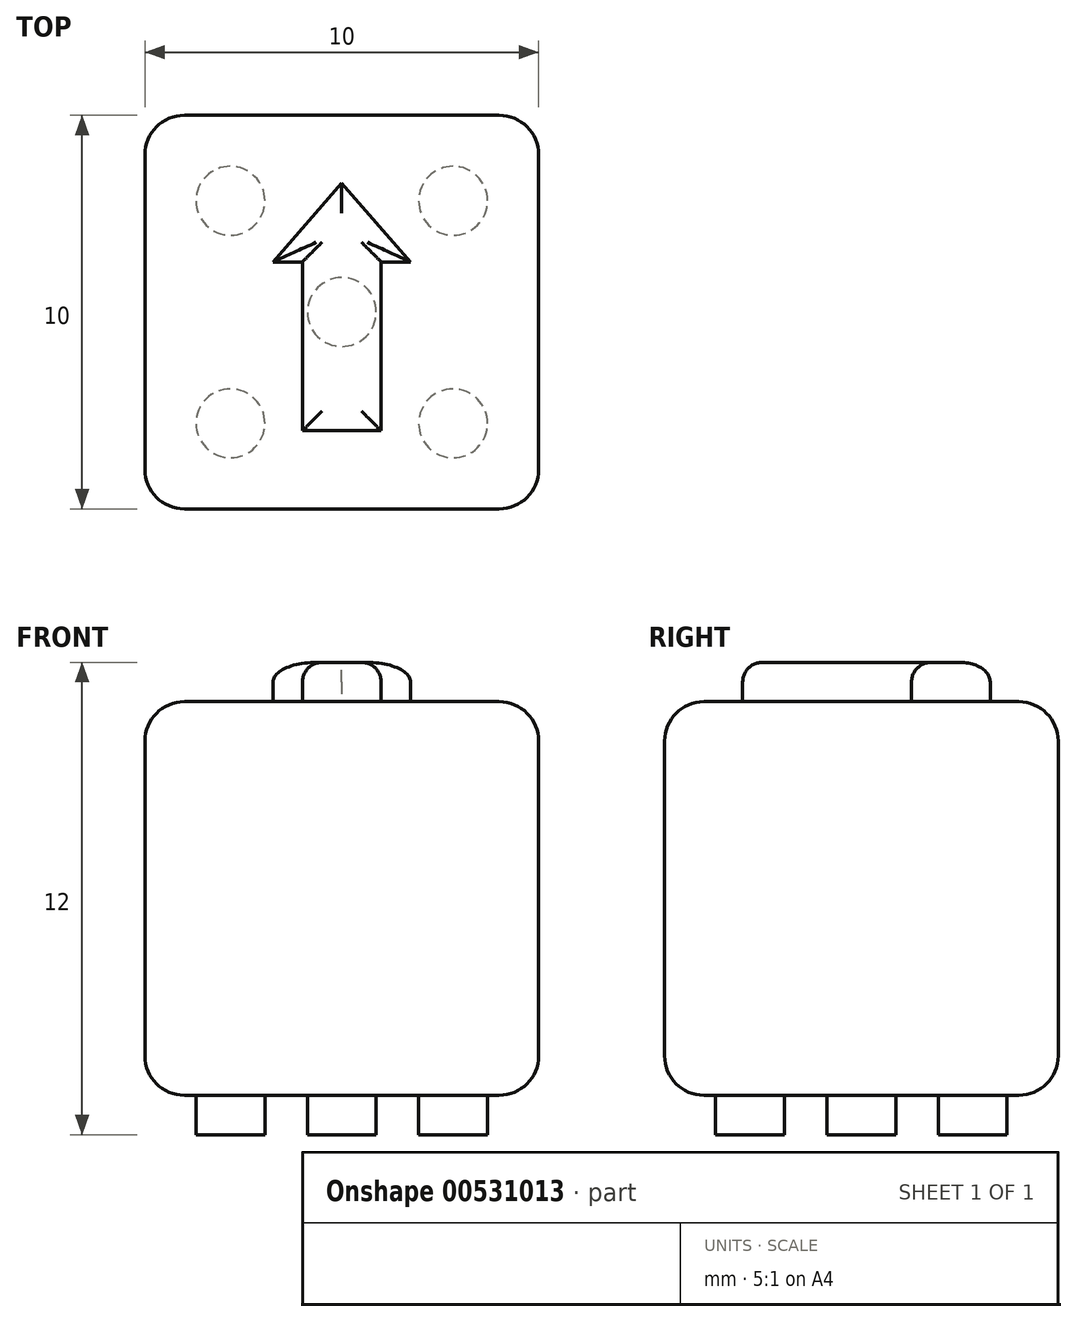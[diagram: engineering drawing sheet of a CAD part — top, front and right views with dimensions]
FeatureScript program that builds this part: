
annotation { "Feature Type Name" : "Feature", "Feature Type Description" : "" }
export const myFeature = defineFeature(function(context is Context, id is Id, definition is map)
    precondition{}
    {
        {
            var Q0;
            Q0=qCreatedBy(makeId("Top.planeOp"),FACE);
            var sketch = newSketch(context, id + "F0", { "sketchPlane" : qUnion([Q0])});
            skLineSegment(sketch, "E0.bottom", {"start": v(5, -5) * mm, "end": v(-5, -5) * mm});
            skLineSegment(sketch, "E0.top", {"start": v(5, 5) * mm, "end": v(-5, 5) * mm});
            skLineSegment(sketch, "E0.left", {"start": v(5, -5) * mm, "end": v(5, 5) * mm});
            skLineSegment(sketch, "E0.right", {"start": v(-5, -5) * mm, "end": v(-5, 5) * mm});
            skPoint(sketch, "E0.middle", {"position": v(0, 0) * mm});
            skLineSegment(sketch, "E1", {"start": v(-5, 5) * mm, "end": v(5, -5) * mm, "construction": true});
            skLineSegment(sketch, "E2", {"start": v(5, 5) * mm, "end": v(-5, -5) * mm, "construction": true});
            skCircle(sketch, "E3", {"center": v(-2.83, 2.83) * mm, "radius": 0.88 * mm});
            skCircle(sketch, "E4", {"center": v(2.83, 2.83) * mm, "radius": 0.88 * mm});
            skCircle(sketch, "E5", {"center": v(2.83, -2.83) * mm, "radius": 0.88 * mm});
            skCircle(sketch, "E6", {"center": v(-2.83, -2.83) * mm, "radius": 0.88 * mm});
            skCircle(sketch, "E7", {"center": v(0, 0) * mm, "radius": 0.88 * mm});
            skSolve(sketch);
        }
        {
            var Q0;
            Q0 = qSketchRegion(id + "F0", true);
            var Q1;
            Q1=makeQuery(id+"F0.imprint","IMPRINT",FACE,{"disambiguationData":[TD([[makeQuery(id+"F0.imprint","IMPRINT",EDGE,{"derivedFrom":sQuery(id+"F0.wireOp",EDGE,"E6")}),1.0]])]});
            var Q2;
            Q2=makeQuery(id+"F0.imprint","IMPRINT",FACE,{"disambiguationData":[TD([[makeQuery(id+"F0.imprint","IMPRINT",EDGE,{"derivedFrom":sQuery(id+"F0.wireOp",EDGE,"E3")}),1.0]])]});
            var Q3;
            Q3=makeQuery(id+"F0.imprint","IMPRINT",FACE,{"disambiguationData":[TD([[makeQuery(id+"F0.imprint","IMPRINT",EDGE,{"derivedFrom":sQuery(id+"F0.wireOp",EDGE,"E4")}),1.0]])]});
            var Q4;
            Q4=makeQuery(id+"F0.imprint","IMPRINT",FACE,{"disambiguationData":[TD([[makeQuery(id+"F0.imprint","IMPRINT",EDGE,{"derivedFrom":sQuery(id+"F0.wireOp",EDGE,"E5")}),1.0]])]});
            var Q5;
            Q5=makeQuery(id+"F0.imprint","IMPRINT",FACE,{"disambiguationData":[TD([[makeQuery(id+"F0.imprint","IMPRINT",EDGE,{"derivedFrom":sQuery(id+"F0.wireOp",EDGE,"E7")}),1.0]])]});
            extrude(context, id + "F1", {"entities" : qUnion([Q0, Q1, Q2, Q3, Q4, Q5]), "depth" : 10 * mm, "offsetDistance" : 25 * mm});
        }
        {
            var Q0;
            Q0=makeQuery(id+"F0.imprint","IMPRINT",FACE,{"disambiguationData":[TD([[makeQuery(id+"F0.imprint","IMPRINT",EDGE,{"derivedFrom":sQuery(id+"F0.wireOp",EDGE,"E4")}),1.0]])]});
            var Q1;
            Q1=makeQuery(id+"F0.imprint","IMPRINT",FACE,{"disambiguationData":[TD([[makeQuery(id+"F0.imprint","IMPRINT",EDGE,{"derivedFrom":sQuery(id+"F0.wireOp",EDGE,"E3")}),1.0]])]});
            var Q2;
            Q2=makeQuery(id+"F0.imprint","IMPRINT",FACE,{"disambiguationData":[TD([[makeQuery(id+"F0.imprint","IMPRINT",EDGE,{"derivedFrom":sQuery(id+"F0.wireOp",EDGE,"E6")}),1.0]])]});
            var Q3;
            Q3=makeQuery(id+"F0.imprint","IMPRINT",FACE,{"disambiguationData":[TD([[makeQuery(id+"F0.imprint","IMPRINT",EDGE,{"derivedFrom":sQuery(id+"F0.wireOp",EDGE,"E5")}),1.0]])]});
            var Q4;
            Q4=makeQuery(id+"F0.imprint","IMPRINT",FACE,{"disambiguationData":[TD([[makeQuery(id+"F0.imprint","IMPRINT",EDGE,{"derivedFrom":sQuery(id+"F0.wireOp",EDGE,"E7")}),1.0]])]});
            extrude(context, id + "F2", {"entities" : qUnion([Q0, Q1, Q2, Q3, Q4]), "operationType" : NewBodyOperationType.ADD, "oppositeDirection" : true, "depth" : 1 * mm, "offsetDistance" : 25 * mm});
        }
        {
            var Q0;
            Q0=makeQuery(id+"F1.opExtrude","SWEPT_EDGE",EDGE,{"disambiguationData":[OSD([sQuery(id+"F0.wireOp",EDGE,"E0.top"),sQuery(id+"F0.wireOp",EDGE,"E0.left")])]});
            var Q1;
            Q1=makeQuery(id+"F1.opExtrude","CAP_EDGE",EDGE,{"disambiguationData":[OSD([sQuery(id+"F0.wireOp",EDGE,"E0.top")])],"isStart":true});
            var Q2;
            Q2=makeQuery(id+"F1.opExtrude","CAP_EDGE",EDGE,{"disambiguationData":[OSD([sQuery(id+"F0.wireOp",EDGE,"E0.left")])],"isStart":true});
            var Q3;
            Q3=makeQuery(id+"F1.opExtrude","CAP_EDGE",EDGE,{"disambiguationData":[OSD([sQuery(id+"F0.wireOp",EDGE,"E0.right")])],"isStart":true});
            var Q4;
            Q4=makeQuery(id+"F1.opExtrude","SWEPT_FACE",FACE,{"disambiguationData":[OSD([sQuery(id+"F0.wireOp",EDGE,"E0.right")])]});
            var Q5;
            Q5=makeQuery(id+"F1.opExtrude","SWEPT_EDGE",EDGE,{"disambiguationData":[OSD([sQuery(id+"F0.wireOp",EDGE,"E0.top"),sQuery(id+"F0.wireOp",EDGE,"E0.right")])]});
            var Q6;
            Q6=makeQuery(id+"F1.opExtrude","CAP_FACE",FACE,{"disambiguationData":[OSD([sQuery(id+"F0.wireOp",EDGE,"E0.bottom"),sQuery(id+"F0.wireOp",EDGE,"E0.top"),sQuery(id+"F0.wireOp",EDGE,"E0.left"),sQuery(id+"F0.wireOp",EDGE,"E0.right")])],"isStart":false});
            var Q7;
            Q7=makeQuery(id+"F1.opExtrude","SWEPT_EDGE",EDGE,{"disambiguationData":[OSD([sQuery(id+"F0.wireOp",EDGE,"E0.bottom"),sQuery(id+"F0.wireOp",EDGE,"E0.left")])]});
            var Q8;
            Q8=makeQuery(id+"F1.opExtrude","CAP_EDGE",EDGE,{"disambiguationData":[OSD([sQuery(id+"F0.wireOp",EDGE,"E0.bottom")])],"isStart":true});
            fillet(context, id + "F3", {"entities" : qUnion([Q0, Q1, Q2, Q3, Q4, Q5, Q6, Q7, Q8]), "radius" : 1 * mm, "tangentPropagation" : true, "allowEdgeOverflow" : false});
        }
        {
            var Q0;
            Q0=makeQuery(id+"F1.opExtrude","CAP_FACE",FACE,{"disambiguationData":[OSD([sQuery(id+"F0.wireOp",EDGE,"E0.bottom"),sQuery(id+"F0.wireOp",EDGE,"E0.top"),sQuery(id+"F0.wireOp",EDGE,"E0.left"),sQuery(id+"F0.wireOp",EDGE,"E0.right")])],"isStart":false});
            var sketch = newSketch(context, id + "F4", { "sketchPlane" : qUnion([Q0])});
            skLineSegment(sketch, "E8", {"start": v(0, 0) * mm, "end": v(1, 0) * mm, "construction": true});
            skLineSegment(sketch, "E9", {"start": v(0, 0) * mm, "end": v(-1, 0) * mm, "construction": true});
            skLineSegment(sketch, "E10", {"start": v(-1, 0) * mm, "end": v(-1, -3.02) * mm});
            skLineSegment(sketch, "E11", {"start": v(-1, -3.02) * mm, "end": v(1, -3.02) * mm});
            skLineSegment(sketch, "E12", {"start": v(1, -3.02) * mm, "end": v(1, 1.27) * mm});
            skLineSegment(sketch, "E13", {"start": v(1, 1.27) * mm, "end": v(1.75, 1.27) * mm});
            skLineSegment(sketch, "E14", {"start": v(1.75, 1.27) * mm, "end": v(0, 3.27) * mm});
            skPoint(sketch, "E14.endSnap0", {"position": v(0, 4) * mm});
            skLineSegment(sketch, "E15", {"start": v(-1.75, 1.27) * mm, "end": v(-1, 1.27) * mm});
            skLineSegment(sketch, "E16", {"start": v(-1, 1.27) * mm, "end": v(-1, 0) * mm});
            skLineSegment(sketch, "E17", {"start": v(-1.75, 1.27) * mm, "end": v(0, 3.27) * mm});
            skSolve(sketch);
        }
        {
            var Q0;
            Q0=makeQuery(id+"F4.imprint","IMPRINT",FACE,{"disambiguationData":[TD([[makeQuery(id+"F4.imprint","IMPRINT",EDGE,{"derivedFrom":sQuery(id+"F4.wireOp",EDGE,"E10")}),1.0]])]});
            extrude(context, id + "F5", {"entities" : qUnion([Q0]), "operationType" : NewBodyOperationType.ADD, "depth" : 1 * mm, "offsetDistance" : 25 * mm});
        }
        {
            var Q0;
            Q0=makeQuery(id+"F5.opExtrude","CAP_EDGE",EDGE,{"disambiguationData":[OSD([sQuery(id+"F4.wireOp",EDGE,"E17")])],"isStart":false});
            var Q1;
            Q1=makeQuery(id+"F5.opExtrude","CAP_FACE",FACE,{"disambiguationData":[OSD([sQuery(id+"F4.wireOp",EDGE,"E10"),sQuery(id+"F4.wireOp",EDGE,"E11"),sQuery(id+"F4.wireOp",EDGE,"E12"),sQuery(id+"F4.wireOp",EDGE,"E13"),sQuery(id+"F4.wireOp",EDGE,"E14"),sQuery(id+"F4.wireOp",EDGE,"E15"),sQuery(id+"F4.wireOp",EDGE,"E16"),sQuery(id+"F4.wireOp",EDGE,"E17")])],"isStart":false});
            fillet(context, id + "F6", {"entities" : qUnion([Q0, Q1]), "radius" : 0.5 * mm, "tangentPropagation" : true, "allowEdgeOverflow" : false});
        }
    });
